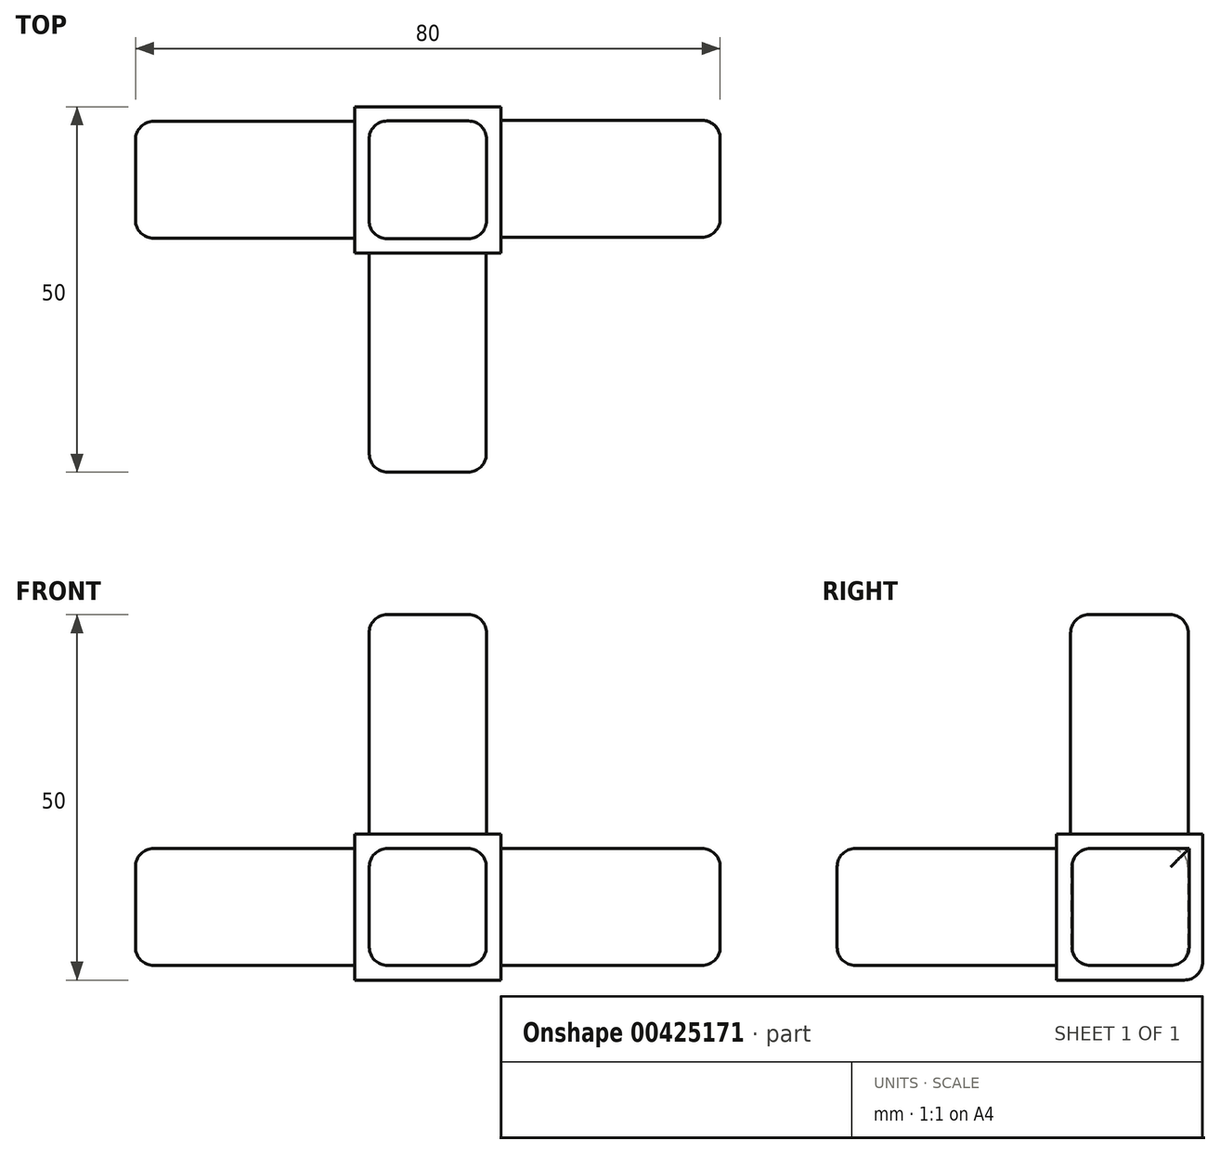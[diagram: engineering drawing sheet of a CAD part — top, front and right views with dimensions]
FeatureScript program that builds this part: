
annotation { "Feature Type Name" : "Feature", "Feature Type Description" : "" }
export const myFeature = defineFeature(function(context is Context, id is Id, definition is map)
    precondition{}
    {
        {
            var Q0;
            Q0=qCreatedBy(makeId("Front.planeOp"),FACE);
            var sketch = newSketch(context, id + "F0", { "sketchPlane" : qUnion([Q0])});
            skLineSegment(sketch, "E0.bottom", {"start": v(-10, -10) * mm, "end": v(10, -10) * mm});
            skLineSegment(sketch, "E0.top", {"start": v(-10, 10) * mm, "end": v(10, 10) * mm});
            skLineSegment(sketch, "E0.left", {"start": v(-10, -10) * mm, "end": v(-10, 10) * mm});
            skLineSegment(sketch, "E0.right", {"start": v(10, -10) * mm, "end": v(10, 10) * mm});
            skPoint(sketch, "E0.middle", {"position": v(0, 0) * mm});
            skLineSegment(sketch, "E1.bottom", {"start": v(-8, -8) * mm, "end": v(8, -8) * mm});
            skLineSegment(sketch, "E1.top", {"start": v(-8, 8) * mm, "end": v(8, 8) * mm});
            skLineSegment(sketch, "E1.left", {"start": v(-8, -8) * mm, "end": v(-8, 8) * mm});
            skLineSegment(sketch, "E1.right", {"start": v(8, -8) * mm, "end": v(8, 8) * mm});
            skSolve(sketch);
        }
        {
            var Q0;
            Q0=makeQuery(id+"F0.imprint","IMPRINT",FACE,{"disambiguationData":[TD([[makeQuery(id+"F0.imprint","IMPRINT",EDGE,{"derivedFrom":sQuery(id+"F0.wireOp",EDGE,"E1.bottom")}),1.0]])]});
            extrude(context, id + "F1", {"entities" : qUnion([Q0]), "depth" : 50 * mm});
        }
        {
            var Q0;
            Q0=qSketchRegion(id+"F0",true);
            extrude(context, id + "F2", {"entities" : qUnion([Q0]), "operationType" : NewBodyOperationType.ADD, "depth" : 20 * mm});
        }
        {
            var Q0;
            Q0=qCreatedBy(makeId("Right.planeOp"),FACE);
            var sketch = newSketch(context, id + "F3", { "sketchPlane" : qUnion([Q0])});
            skLineSegment(sketch, "E2.bottom", {"start": v(-1.85, -8) * mm, "end": v(-17.85, -8) * mm});
            skLineSegment(sketch, "E2.top", {"start": v(-1.85, 8) * mm, "end": v(-17.85, 8) * mm});
            skLineSegment(sketch, "E2.left", {"start": v(-1.85, -8) * mm, "end": v(-1.85, 8) * mm});
            skLineSegment(sketch, "E2.right", {"start": v(-17.85, -8) * mm, "end": v(-17.85, 8) * mm});
            skPoint(sketch, "E2.middle", {"position": v(-9.85, 0) * mm});
            skSolve(sketch);
        }
        {
            var Q0;
            Q0=qSketchRegion(id+"F3",true);
            extrude(context, id + "F4", {"entities" : qUnion([Q0]), "operationType" : NewBodyOperationType.ADD, "depth" : 40 * mm});
        }
        {
            var Q0;
            Q0=qCreatedBy(makeId("Right.planeOp"),FACE);
            var sketch = newSketch(context, id + "F5", { "sketchPlane" : qUnion([Q0])});
            skLineSegment(sketch, "E3.bottom", {"start": v(-2, -8) * mm, "end": v(-18, -8) * mm});
            skLineSegment(sketch, "E3.top", {"start": v(-2, 8) * mm, "end": v(-18, 8) * mm});
            skLineSegment(sketch, "E3.left", {"start": v(-2, -8) * mm, "end": v(-2, 8) * mm});
            skLineSegment(sketch, "E3.right", {"start": v(-18, -8) * mm, "end": v(-18, 8) * mm});
            skPoint(sketch, "E3.middle", {"position": v(-10, 0) * mm});
            skSolve(sketch);
        }
        {
            var Q0;
            Q0 = qSketchRegion(id + "F5", true);
            extrude(context, id + "F6", {"entities" : qUnion([Q0]), "operationType" : NewBodyOperationType.ADD, "oppositeDirection" : true, "depth" : 40 * mm});
        }
        {
            var Q0;
            Q0=qCreatedBy(makeId("Top.planeOp"),FACE);
            var sketch = newSketch(context, id + "F7", { "sketchPlane" : qUnion([Q0])});
            skLineSegment(sketch, "E4.bottom", {"start": v(-8.05, -18.05) * mm, "end": v(8.05, -18.05) * mm});
            skLineSegment(sketch, "E4.top", {"start": v(-8.05, -1.95) * mm, "end": v(8.05, -1.95) * mm});
            skLineSegment(sketch, "E4.left", {"start": v(-8.05, -18.05) * mm, "end": v(-8.05, -1.95) * mm});
            skLineSegment(sketch, "E4.right", {"start": v(8.05, -18.05) * mm, "end": v(8.05, -1.95) * mm});
            skPoint(sketch, "E4.middle", {"position": v(0, -10) * mm});
            skSolve(sketch);
        }
        {
            var Q0;
            Q0 = qSketchRegion(id + "F7", true);
            extrude(context, id + "F8", {"entities" : qUnion([Q0]), "operationType" : NewBodyOperationType.ADD, "depth" : 40 * mm});
        }
        {
            var Q0;
            Q0=makeQuery(id+"F2.opExtrude","CAP_EDGE",EDGE,{"disambiguationData":[OSD([sQuery(id+"F0.wireOp",EDGE,"E0.bottom")])],"isStart":true});
            var Q1;
            Q1=makeQuery(id+"F6.opExtrude","SWEPT_EDGE",EDGE,{"disambiguationData":[OSD([sQuery(id+"F5.wireOp",EDGE,"E3.bottom"),sQuery(id+"F5.wireOp",EDGE,"E3.left")])]});
            var Q2;
            Q2=makeQuery(id+"F6.opExtrude","SWEPT_EDGE",EDGE,{"disambiguationData":[OSD([sQuery(id+"F5.wireOp",EDGE,"E3.bottom"),sQuery(id+"F5.wireOp",EDGE,"E3.right")])]});
            var Q3;
            Q3=makeQuery(id+"F6.opExtrude","SWEPT_EDGE",EDGE,{"disambiguationData":[OSD([sQuery(id+"F5.wireOp",EDGE,"E3.top"),sQuery(id+"F5.wireOp",EDGE,"E3.left")])]});
            var Q4;
            Q4=makeQuery(id+"F6.opExtrude","SWEPT_EDGE",EDGE,{"disambiguationData":[OSD([sQuery(id+"F5.wireOp",EDGE,"E3.top"),sQuery(id+"F5.wireOp",EDGE,"E3.right")])]});
            var Q5;
            Q5=makeQuery(id+"F6.opExtrude","CAP_FACE",FACE,{"disambiguationData":[OSD([sQuery(id+"F5.wireOp",EDGE,"E3.bottom"),sQuery(id+"F5.wireOp",EDGE,"E3.top"),sQuery(id+"F5.wireOp",EDGE,"E3.left"),sQuery(id+"F5.wireOp",EDGE,"E3.right")])],"isStart":false});
            var Q6;
            Q6=makeQuery(id+"F8.opExtrude","SWEPT_EDGE",EDGE,{"disambiguationData":[OSD([sQuery(id+"F7.wireOp",EDGE,"E4.bottom"),sQuery(id+"F7.wireOp",EDGE,"E4.left")])]});
            var Q7;
            Q7=makeQuery(id+"F8.opExtrude","CAP_EDGE",EDGE,{"disambiguationData":[OSD([sQuery(id+"F7.wireOp",EDGE,"E4.bottom")])],"isStart":false});
            var Q8;
            Q8=makeQuery(id+"F8.opExtrude","CAP_FACE",FACE,{"disambiguationData":[OSD([sQuery(id+"F7.wireOp",EDGE,"E4.bottom"),sQuery(id+"F7.wireOp",EDGE,"E4.top"),sQuery(id+"F7.wireOp",EDGE,"E4.left"),sQuery(id+"F7.wireOp",EDGE,"E4.right")])],"isStart":false});
            var Q9;
            Q9=makeQuery(id+"F8.opExtrude","SWEPT_EDGE",EDGE,{"disambiguationData":[OSD([sQuery(id+"F7.wireOp",EDGE,"E4.top"),sQuery(id+"F7.wireOp",EDGE,"E4.left")])]});
            var Q10;
            Q10=makeQuery(id+"F8.opExtrude","SWEPT_EDGE",EDGE,{"disambiguationData":[OSD([sQuery(id+"F7.wireOp",EDGE,"E4.top"),sQuery(id+"F7.wireOp",EDGE,"E4.right")])]});
            var Q11;
            Q11=makeQuery(id+"F8.opExtrude","SWEPT_EDGE",EDGE,{"disambiguationData":[OSD([sQuery(id+"F7.wireOp",EDGE,"E4.bottom"),sQuery(id+"F7.wireOp",EDGE,"E4.right")])]});
            var Q12;
            Q12=makeQuery(id+"F1.opExtrude","SWEPT_EDGE",EDGE,{"disambiguationData":[OSD([sQuery(id+"F0.wireOp",EDGE,"E1.top"),sQuery(id+"F0.wireOp",EDGE,"E1.left")])]});
            var Q13;
            Q13=makeQuery(id+"F1.opExtrude","CAP_EDGE",EDGE,{"disambiguationData":[OSD([sQuery(id+"F0.wireOp",EDGE,"E1.top")])],"isStart":false});
            var Q14;
            Q14=makeQuery(id+"F1.opExtrude","SWEPT_EDGE",EDGE,{"disambiguationData":[OSD([sQuery(id+"F0.wireOp",EDGE,"E1.top"),sQuery(id+"F0.wireOp",EDGE,"E1.right")])]});
            var Q15;
            Q15=makeQuery(id+"F1.opExtrude","CAP_FACE",FACE,{"disambiguationData":[OSD([sQuery(id+"F0.wireOp",EDGE,"E1.bottom"),sQuery(id+"F0.wireOp",EDGE,"E1.top"),sQuery(id+"F0.wireOp",EDGE,"E1.left"),sQuery(id+"F0.wireOp",EDGE,"E1.right")])],"isStart":false});
            var Q16;
            Q16=makeQuery(id+"F4.opExtrude","SWEPT_EDGE",EDGE,{"disambiguationData":[OSD([sQuery(id+"F3.wireOp",EDGE,"E2.top"),sQuery(id+"F3.wireOp",EDGE,"E2.right")])]});
            var Q17;
            Q17=makeQuery(id+"F4.opExtrude","SWEPT_EDGE",EDGE,{"disambiguationData":[OSD([sQuery(id+"F3.wireOp",EDGE,"E2.bottom"),sQuery(id+"F3.wireOp",EDGE,"E2.right")])]});
            var Q18;
            Q18=makeQuery(id+"F4.opExtrude","CAP_FACE",FACE,{"disambiguationData":[OSD([sQuery(id+"F3.wireOp",EDGE,"E2.bottom"),sQuery(id+"F3.wireOp",EDGE,"E2.top"),sQuery(id+"F3.wireOp",EDGE,"E2.left"),sQuery(id+"F3.wireOp",EDGE,"E2.right")])],"isStart":false});
            var Q19;
            Q19=makeQuery(id+"F1.opExtrude","SWEPT_EDGE",EDGE,{"disambiguationData":[OSD([sQuery(id+"F0.wireOp",EDGE,"E1.bottom"),sQuery(id+"F0.wireOp",EDGE,"E1.right")])]});
            var Q20;
            Q20=makeQuery(id+"F1.opExtrude","SWEPT_EDGE",EDGE,{"disambiguationData":[OSD([sQuery(id+"F0.wireOp",EDGE,"E1.bottom"),sQuery(id+"F0.wireOp",EDGE,"E1.left")])]});
            var Q21;
            Q21=makeQuery(id+"F4.opExtrude","SWEPT_EDGE",EDGE,{"disambiguationData":[OSD([sQuery(id+"F3.wireOp",EDGE,"E2.bottom"),sQuery(id+"F3.wireOp",EDGE,"E2.left")])]});
            fillet(context, id + "F9", {"entities" : qUnion([Q0, Q1, Q2, Q3, Q4, Q5, Q6, Q7, Q8, Q9, Q10, Q11, Q12, Q13, Q14, Q15, Q16, Q17, Q18, Q19, Q20, Q21]), "radius" : 2.5 * mm, "tangentPropagation" : true, "allowEdgeOverflow" : false});
        }
    });
